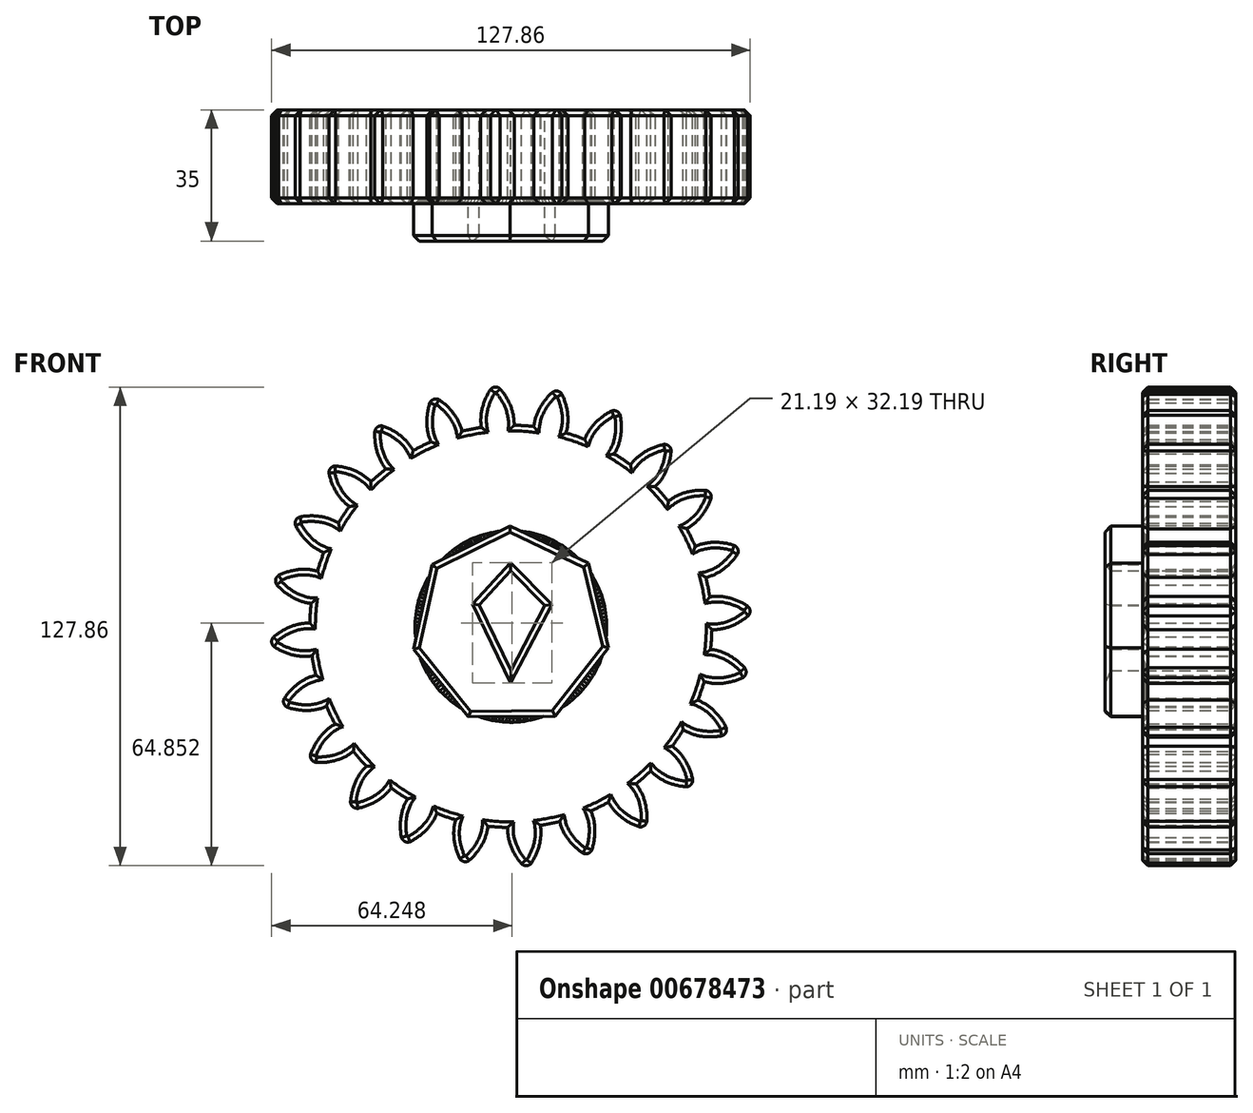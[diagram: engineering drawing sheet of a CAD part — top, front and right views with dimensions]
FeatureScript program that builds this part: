
annotation { "Feature Type Name" : "Feature", "Feature Type Description" : "" }
export const myFeature = defineFeature(function(context is Context, id is Id, definition is map)
    precondition{}
    {
        {
            var Q0;
            Q0=qCreatedBy(makeId("Front.planeOp"),FACE);
            var sketch = newSketch(context, id + "F0", { "sketchPlane" : qUnion([Q0])});
            skCircle(sketch, "E0", {"center": v(0, 0) * mm, "radius": 53.72 * mm});
            skCircle(sketch, "E1", {"center": v(0, 0) * mm, "radius": 58.67 * mm, "construction": true});
            skCircle(sketch, "E2", {"center": v(0, 0) * mm, "radius": 63.5 * mm, "construction": true});
            skLineSegment(sketch, "E3", {"start": v(0, 0) * mm, "end": v(0, 84.45) * mm, "construction": true});
            skLineSegment(sketch, "E4", {"start": v(0, 0) * mm, "end": v(-5.65, 86.22) * mm, "construction": true});
            skLineSegment(sketch, "E5", {"start": v(0, 58.67) * mm, "end": v(-58.15, 58.67) * mm, "construction": true});
            skLineSegment(sketch, "E6", {"start": v(0, 58.67) * mm, "end": v(-56.77, 38.01) * mm, "construction": true});
            skCircle(sketch, "E7", {"center": v(0, 0) * mm, "radius": 55.14 * mm, "construction": true});
            skCircle(sketch, "E8", {"center": v(0, 58.67) * mm, "radius": 14.6 * mm, "construction": true});
            skCircle(sketch, "E9", {"center": v(-13.72, 53.68) * mm, "radius": 14.6 * mm, "construction": true});
            skArc(sketch, "E10", {"start": v(0, 58.67) * mm, "mid": v(-1.23, 61.18) * mm, "end": v(-2.86, 63.44) * mm});
            skArc(sketch, "E11", {"start": v(0.88, 53.71) * mm, "mid": v(0.68, 56.24) * mm, "end": v(0, 58.67) * mm});
            skArc(sketch, "E12.MirrorCS", {"start": v(-7.66, 58.17) * mm, "mid": v(-6.77, 60.81) * mm, "end": v(-5.45, 63.27) * mm});
            skArc(sketch, "E13.MirrorCS", {"start": v(-7.88, 53.14) * mm, "mid": v(-8.02, 55.67) * mm, "end": v(-7.66, 58.17) * mm});
            skArc(sketch, "E14", {"start": v(-2.86, 63.44) * mm, "mid": v(-4.19, 63.93) * mm, "end": v(-5.45, 63.27) * mm});
            skCircle(sketch, "E15.cCircle", {"center": v(0, 0) * mm, "radius": 24.1 * mm, "construction": true});
            skLineSegment(sketch, "E15.0", {"start": v(-0.21, 26.75) * mm, "end": v(20.78, 16.84) * mm});
            skLineSegment(sketch, "E15.1", {"start": v(20.78, 16.84) * mm, "end": v(26.12, -5.75) * mm});
            skLineSegment(sketch, "E15.2", {"start": v(26.12, -5.75) * mm, "end": v(11.8, -24) * mm});
            skLineSegment(sketch, "E15.3", {"start": v(11.8, -24) * mm, "end": v(-11.42, -24.2) * mm});
            skLineSegment(sketch, "E15.4", {"start": v(-11.42, -24.2) * mm, "end": v(-26.03, -6.16) * mm});
            skLineSegment(sketch, "E15.5", {"start": v(-26.03, -6.16) * mm, "end": v(-21.04, 16.51) * mm});
            skLineSegment(sketch, "E15.6", {"start": v(-21.04, 16.51) * mm, "end": v(-0.21, 26.75) * mm});
            skPoint(sketch, "E15.0.midPoint", {"position": v(10.29, 21.8) * mm});
            skLineSegment(sketch, "E16", {"start": v(-8.48, 5.72) * mm, "end": v(0, 14.9) * mm});
            skLineSegment(sketch, "E17", {"start": v(-0.1, 14.9) * mm, "end": v(9.08, 5.53) * mm});
            skLineSegment(sketch, "E18", {"start": v(9.08, 5.53) * mm, "end": v(0, -11.84) * mm});
            skLineSegment(sketch, "E19", {"start": v(0, -11.84) * mm, "end": v(-8.48, 5.72) * mm});
            skSolve(sketch);
        }
        {
            var Q0;
            {var subQ0=sQuery(id+"F0.wireOp",EDGE,"E0");var subQ1=makeQuery(id+"F0.imprint","INTERSECT",VERTEX,{"derivedFrom":[subQ0,sQuery(id+"F0.wireOp",EDGE,"E11")]});Q0=makeQuery(id+"F0.imprint","IMPRINT",FACE,{"disambiguationData":[TD([[makeQuery(id+"F0.imprint","IMPRINT",EDGE,{"disambiguationData":[TD([[subQ1,-1.0]])],"derivedFrom":subQ0}),1.0]])]});}
            var Q1;
            Q1=makeQuery(id+"F0.imprint","IMPRINT",FACE,{"disambiguationData":[TD([[makeQuery(id+"F0.imprint","IMPRINT",EDGE,{"derivedFrom":sQuery(id+"F0.wireOp",EDGE,"E10")}),1.0]])]});
            var Q2;
            Q2=makeQuery(id+"F0.imprint","IMPRINT",FACE,{"disambiguationData":[TD([[makeQuery(id+"F0.imprint","IMPRINT",EDGE,{"derivedFrom":sQuery(id+"F0.wireOp",EDGE,"KPl7GWz1-QKYE-BqnT-suHZ-WVKqvGR7DCmq")}),1.0]])]});
            extrude(context, id + "F1", {"entities" : qUnion([Q0, Q1, Q2]), "depth" : 25 * mm, "offsetDistance" : 25 * mm});
        }
        {
            var Q0;
            Q0=makeQuery(id+"F1.opExtrude","CAP_FACE",FACE,{"disambiguationData":[OSD([sQuery(id+"F0.wireOp",EDGE,"E0"),sQuery(id+"F0.wireOp",EDGE,"E10"),sQuery(id+"F0.wireOp",EDGE,"E11"),sQuery(id+"F0.wireOp",EDGE,"E12.MirrorCS"),sQuery(id+"F0.wireOp",EDGE,"E13.MirrorCS"),sQuery(id+"F0.wireOp",EDGE,"E14"),sQuery(id+"F0.wireOp",EDGE,"nStCvYip-9NVA-ghG0-urJP-zkuzE5h75Hni"),sQuery(id+"F0.wireOp",EDGE,"fEGYOMVp-H6J9-NFKH-Mf8a-BV4wDKhmTZL4"),sQuery(id+"F0.wireOp",EDGE,"6OWbR7jb-1kZp-3J37-VbOm-1KsBZJzDgDaf"),sQuery(id+"F0.wireOp",EDGE,"06dQeBHX-lVnL-JT1g-5sLK-Wjo0wTyQ7Brg")])],"isStart":false});
            chamfer(context, id + "F2", {"entities" : qUnion([Q0]), "width" : 1.5 * mm, "tangentPropagation" : true});
        }
        {
            var Q0;
            Q0=makeQuery(id+"F1.opExtrude","SWEPT_BODY",BODY,{"disambiguationData":[OSD([sQuery(id+"F0.wireOp",EDGE,"E0"),sQuery(id+"F0.wireOp",EDGE,"E10"),sQuery(id+"F0.wireOp",EDGE,"E11"),sQuery(id+"F0.wireOp",EDGE,"E12.MirrorCS"),sQuery(id+"F0.wireOp",EDGE,"E13.MirrorCS"),sQuery(id+"F0.wireOp",EDGE,"E14")])]});
            var Q1;
            Q1=makeQuery(id+"F1.opExtrude","SWEPT_FACE",FACE,{"disambiguationData":[OSD([sQuery(id+"F0.wireOp",EDGE,"E0")])]});
            circularPattern(context, id + "F3", {"entities" : qUnion([Q0]), "axis" : qUnion([Q1]), "angle" : 360 * degree, "instanceCount" : 24, "equalSpace" : true});
        }
        {
            var Q0;
            Q0=makeQuery(id+"F0.imprint","IMPRINT",FACE,{"disambiguationData":[TD([[makeQuery(id+"F0.imprint","IMPRINT",EDGE,{"derivedFrom":sQuery(id+"F0.wireOp",EDGE,"E15.0")}),-1.0]])]});
            extrude(context, id + "F4", {"entities" : qUnion([Q0]), "operationType" : NewBodyOperationType.ADD, "depth" : 35 * mm, "offsetDistance" : 25 * mm});
        }
        {
            var Q0;
            Q0=makeQuery(id+"F4.opExtrude","CAP_FACE",FACE,{"disambiguationData":[OSD([sQuery(id+"F0.wireOp",EDGE,"E15.0"),sQuery(id+"F0.wireOp",EDGE,"E15.1"),sQuery(id+"F0.wireOp",EDGE,"E15.2"),sQuery(id+"F0.wireOp",EDGE,"E15.3"),sQuery(id+"F0.wireOp",EDGE,"E15.4"),sQuery(id+"F0.wireOp",EDGE,"E15.5"),sQuery(id+"F0.wireOp",EDGE,"E15.6"),sQuery(id+"F0.wireOp",EDGE,"E16"),sQuery(id+"F0.wireOp",EDGE,"E17"),sQuery(id+"F0.wireOp",EDGE,"E18"),sQuery(id+"F0.wireOp",EDGE,"E19")])],"isStart":false});
            var Q1;
            {var subQ0=sQuery(id+"F0.wireOp",EDGE,"E15.6");var subQ1=sQuery(id+"F0.wireOp",EDGE,"E15.5");var subQ2=sQuery(id+"F0.wireOp",EDGE,"E15.4");var subQ3=sQuery(id+"F0.wireOp",EDGE,"E15.3");var subQ4=sQuery(id+"F0.wireOp",EDGE,"E15.2");var subQ5=sQuery(id+"F0.wireOp",EDGE,"E15.1");var subQ6=sQuery(id+"F0.wireOp",EDGE,"E15.0");var subQ7=makeQuery(id+"F1.opExtrude","CAP_FACE",FACE,{"disambiguationData":[OSD([sQuery(id+"F0.wireOp",EDGE,"E0"),sQuery(id+"F0.wireOp",EDGE,"E10"),sQuery(id+"F0.wireOp",EDGE,"E11"),sQuery(id+"F0.wireOp",EDGE,"E12.MirrorCS"),sQuery(id+"F0.wireOp",EDGE,"E13.MirrorCS"),sQuery(id+"F0.wireOp",EDGE,"E14"),subQ6,subQ5,subQ4,subQ3,subQ2,subQ1,subQ0])],"isStart":true});Q1=makeQuery(id+"F4.boolean.opBoolean","MERGE",FACE,{"derivedFrom":[subQ7,makeQuery(id+"F3.opPattern","COPY",FACE,{"derivedFrom":subQ7,"instanceName":"1"}),makeQuery(id+"F3.opPattern","COPY",FACE,{"derivedFrom":subQ7,"instanceName":"2"}),makeQuery(id+"F3.opPattern","COPY",FACE,{"derivedFrom":subQ7,"instanceName":"3"}),makeQuery(id+"F3.opPattern","COPY",FACE,{"derivedFrom":subQ7,"instanceName":"4"}),makeQuery(id+"F3.opPattern","COPY",FACE,{"derivedFrom":subQ7,"instanceName":"5"}),makeQuery(id+"F3.opPattern","COPY",FACE,{"derivedFrom":subQ7,"instanceName":"6"}),makeQuery(id+"F3.opPattern","COPY",FACE,{"derivedFrom":subQ7,"instanceName":"7"}),makeQuery(id+"F3.opPattern","COPY",FACE,{"derivedFrom":subQ7,"instanceName":"8"}),makeQuery(id+"F3.opPattern","COPY",FACE,{"derivedFrom":subQ7,"instanceName":"9"}),makeQuery(id+"F3.opPattern","COPY",FACE,{"derivedFrom":subQ7,"instanceName":"10"}),makeQuery(id+"F3.opPattern","COPY",FACE,{"derivedFrom":subQ7,"instanceName":"11"}),makeQuery(id+"F3.opPattern","COPY",FACE,{"derivedFrom":subQ7,"instanceName":"12"}),makeQuery(id+"F3.opPattern","COPY",FACE,{"derivedFrom":subQ7,"instanceName":"13"}),makeQuery(id+"F3.opPattern","COPY",FACE,{"derivedFrom":subQ7,"instanceName":"14"}),makeQuery(id+"F3.opPattern","COPY",FACE,{"derivedFrom":subQ7,"instanceName":"15"}),makeQuery(id+"F3.opPattern","COPY",FACE,{"derivedFrom":subQ7,"instanceName":"16"}),makeQuery(id+"F3.opPattern","COPY",FACE,{"derivedFrom":subQ7,"instanceName":"17"}),makeQuery(id+"F3.opPattern","COPY",FACE,{"derivedFrom":subQ7,"instanceName":"18"}),makeQuery(id+"F3.opPattern","COPY",FACE,{"derivedFrom":subQ7,"instanceName":"19"}),makeQuery(id+"F3.opPattern","COPY",FACE,{"derivedFrom":subQ7,"instanceName":"20"}),makeQuery(id+"F3.opPattern","COPY",FACE,{"derivedFrom":subQ7,"instanceName":"21"}),makeQuery(id+"F3.opPattern","COPY",FACE,{"derivedFrom":subQ7,"instanceName":"22"}),makeQuery(id+"F3.opPattern","COPY",FACE,{"derivedFrom":subQ7,"instanceName":"23"}),makeQuery(id+"F4.opExtrude","CAP_FACE",FACE,{"disambiguationData":[OSD([subQ6,subQ5,subQ4,subQ3,subQ2,subQ1,subQ0,sQuery(id+"F0.wireOp",EDGE,"E16"),sQuery(id+"F0.wireOp",EDGE,"E17"),sQuery(id+"F0.wireOp",EDGE,"E18"),sQuery(id+"F0.wireOp",EDGE,"E19")])],"isStart":true})]});}
            chamfer(context, id + "F5", {"entities" : qUnion([Q0, Q1]), "width" : 1.5 * mm, "tangentPropagation" : true});
        }
    });
